# Revit family: Rolling-Security-Grille_Cookson_Visionaire_Between-Jamb-Mount
name_source: partatom
category: Specialty Equipment
revit_build: Autodesk Revit 2017 (Build: 20190508_0315(x64)
units: mm (PartAtom-declared; Revit-internal decimal feet)

## family parameters
Always vertical = Yes
Cut with Voids When Loaded = No
OmniClass Number = 23.25.40.17.21
OmniClass Title = Coiling Partitions
Part Type = Normal
Room Calculation Point = No
Round Connector Dimension = Use Diameter
Shared = No
Work Plane-Based = Yes

## types (1)
- ESG - Create Custom Size
    Actual Height = 10' - 0"
    Actual Width = 10' - 0"
    Assembly Code = B2030410
    Bottom Bar = Metal -  Cookson -Aluminum, mill finish (non-curtain components)
    Chain Length = 8' - 0"
    Curtain = Metal -  Cookson -Aluminum, mill finish (curtain only)
    Custom Size Warning = Size Available
    Default Elevation = 0"
    Description = Built to order, open curtain grilles provide security, visual access of separated areas.
    Edition number = 1
    Guides = Metal -  Cookson -Aluminum, mill finish (non-curtain components)
    Hmax = 20' - 0"
    Hmin = 4' - 0"
    Hood = Metal -  Cookson -Aluminum, mill finish (non-curtain components)
    Hood Depth = 1' - 8"
    Hood Height = 1' - 6"
    Largest Dimension = 10' - 0"
    Manufacturer = Cookson
    Model = ESG
    Mounting = Between Jambs
    Opening Height = 10' - 0"
    Opening Width = 10' - 0"
    Operator = Metal -  Cookson -Aluminum, mill finish (non-curtain components)
    Product Guid = a5d4a5c5-dd03-4e2e-b036-32e5c314bafe
    Product data url = https://bimobject.com
    Sizing Disclaimer = Openings up to 30' wide and 20' high are standard construction. Consult Manufacturer for larger sizes
    Tube Height = 12' - 6"
    URL = https://www.cooksondoor.com
    Wall Construction = Self supporting tubes; Mansonry, Steel or Wood
    Wmax = 30' - 0"
    Wmin = 4' - 0"
    Zone 1 = No
    Zone 2 = No
    Zone 3 = No
    Zone 4 = No
    Zone 5 = Yes
    Zone 6 = No
    Zone 7 = No
    Zone 8 = No
    a = 6 1/2"
    b = 1' - 5"

## geometry (parser evidence)
native form markers: Blend x6, Sweep x2
no freeform markers — native parametric forms only
